# Revit family: TV-200
name_source: partatom
category: Plumbing Fixtures
revit_build: Autodesk Revit 2014 (Build: 20130308_1515(x64)
units: mm (PartAtom-declared; Revit-internal decimal feet)

## types (1)
- TV-200
    Batteries = DL-223 Duracell Lithium Battery Or CRP2 (Panasonic)
    CW Connection = Yes
    Certification = http://www.helvex.com.mx
    Chrome = Brass Chromed
    Description = Nuva Battery Operated Electronic Wall
    Detection Range = 1.9" (50 mm) - 9.4" (240 mm)
    Documentation = http://www.helvex.com.mx
    Features = Operates With 6V Lithium Battery, Swivel Spout, Features Infrared Sensor, 15 s Time Tolerance 20% -+
    Feeding Voltage = 6 V
    HW Connection = Yes
    Inlet Threads = ½" - 14 NPSM
    Instructive = http://www.helvex.com.mx
    Manufacturer = Helvex
    Max. Water Flow = 0.5 gal/min
    Max. Working Pressure = 85.3 psi
    Min. Working Pressure = 5.7 psi
    Model = TV-200
    Type Comments = Electronic Line
    URL = http://www.helvex.com.mx

## geometry (parser evidence)
native form markers: Sweep x3
no freeform markers — native parametric forms only
